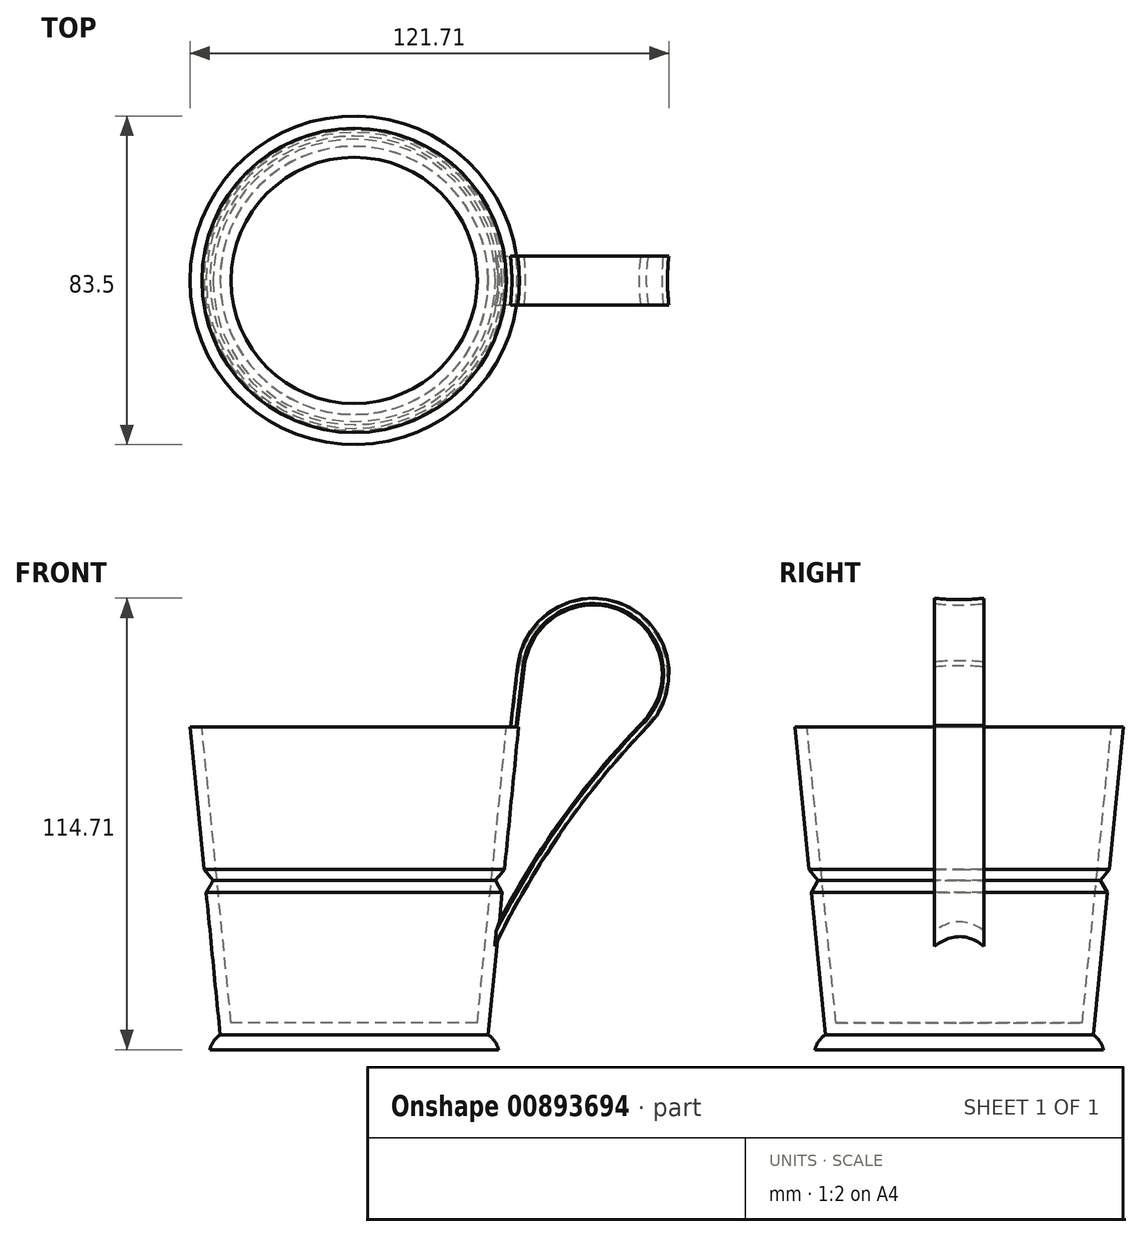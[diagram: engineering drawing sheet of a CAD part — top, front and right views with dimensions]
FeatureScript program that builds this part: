
annotation { "Feature Type Name" : "Feature", "Feature Type Description" : "" }
export const myFeature = defineFeature(function(context is Context, id is Id, definition is map)
    precondition{}
    {
        {
            var Q0;
            Q0=qCreatedBy(makeId("Top.planeOp"),FACE);
            var sketch = newSketch(context, id + "F0", { "sketchPlane" : qUnion([Q0])});
            skCircle(sketch, "E0", {"center": v(0, 0) * mm, "radius": 33.02 * mm});
            skSolve(sketch);
        }
        {
            var Q0;
            Q0=makeQuery(id+"F0.imprint","IMPRINT",FACE,{"disambiguationData":[TD([[makeQuery(id+"F0.imprint","IMPRINT",EDGE,{"derivedFrom":sQuery(id+"F0.wireOp",EDGE,"E0")}),1.0]])]});
            extrude(context, id + "F1", {"entities" : qUnion([Q0]), "depth" : 78.23 * mm, "offsetDistance" : 25.4 * mm, "hasDraft" : true, "draftAngle" : 5.63 * degree});
        }
        {
            var Q0;
            Q0=qCreatedBy(makeId("Front.planeOp"),FACE);
            var sketch = newSketch(context, id + "F2", { "sketchPlane" : qUnion([Q0])});
            skLineSegment(sketch, "E1", {"start": v(0, 0) * mm, "end": v(-34.1, 0) * mm});
            skArc(sketch, "E2", {"start": v(-34.1, 0) * mm, "mid": v(-35.73, -1.6) * mm, "end": v(-36.65, -3.7) * mm});
            skLineSegment(sketch, "E3", {"start": v(-36.65, -3.7) * mm, "end": v(0, -3.7) * mm});
            skLineSegment(sketch, "E4", {"start": v(0, -3.7) * mm, "end": v(0, 0) * mm});
            skSolve(sketch);
        }
        {
            var Q0;
            Q0=makeQuery(id+"F1.opExtrude","CAP_FACE",FACE,{"disambiguationData":[OSD([sQuery(id+"F0.wireOp",EDGE,"E0")])],"isStart":true});
            var sketch = newSketch(context, id + "F3", { "sketchPlane" : qUnion([Q0])});
            skCircle(sketch, "E5", {"center": v(0, 0) * mm, "radius": 34.04 * mm});
            skSolve(sketch);
        }
        {
            var Q0;
            Q0=makeQuery(id+"F3.imprint","IMPRINT",FACE,{"disambiguationData":[TD([[makeQuery(id+"F3.imprint","IMPRINT",EDGE,{"derivedFrom":sQuery(id+"F3.wireOp",EDGE,"E5")}),1.0]])]});
            extrude(context, id + "F4", {"entities" : qUnion([Q0]), "operationType" : NewBodyOperationType.ADD, "oppositeDirection" : true, "depth" : 78.23 * mm, "offsetDistance" : 25.4 * mm, "hasDraft" : true, "draftAngle" : 5.63 * degree});
        }
        {
            var Q0;
            {var subQ0=sQuery(id+"F0.wireOp",EDGE,"E0");Q0=makeQuery(id+"F4.boolean.opBoolean","MERGE",FACE,{"derivedFrom":[makeQuery(id+"F1.opExtrude","CAP_FACE",FACE,{"disambiguationData":[OSD([subQ0])],"isStart":false}),makeQuery(id+"F4.opExtrude","CAP_FACE",FACE,{"disambiguationData":[OSD([subQ0,sQuery(id+"F3.wireOp",EDGE,"E5")])],"isStart":false})]});}
            shell(context, id + "F5", {"entities" : qUnion([Q0]), "thickness" : 3.05 * mm});
        }
        {
            var Q0;
            Q0=qCreatedBy(makeId("Front.planeOp"),FACE);
            var sketch = newSketch(context, id + "F6", { "sketchPlane" : qUnion([Q0])});
            skLineSegment(sketch, "E6", {"start": v(0, 91.35) * mm, "end": v(0, 0) * mm});
            skLineSegment(sketch, "E7", {"start": v(5.67, 39.25) * mm, "end": v(5.67, 0.13) * mm});
            skLineSegment(sketch, "E8", {"start": v(37.88, 39.3) * mm, "end": v(35.84, 39.3) * mm});
            skLineSegment(sketch, "E9", {"start": v(35.84, 39.25) * mm, "end": v(38.45, 42.44) * mm});
            skLineSegment(sketch, "E10", {"start": v(38.45, 42.44) * mm, "end": v(37.82, 35.82) * mm});
            skLineSegment(sketch, "E11", {"start": v(37.82, 35.82) * mm, "end": v(35.84, 39.25) * mm});
            skSolve(sketch);
        }
        {
            var Q0;
            Q0 = qSketchRegion(id + "F6", true);
            var Q1;
            Q1=sQuery(id+"F6.wireOp",EDGE,"E6");
            revolve(context, id + "F7", {"operationType" : NewBodyOperationType.REMOVE, "surfaceOperationType" : NewSurfaceOperationType.NEW, "entities" : qUnion([Q0]), "axis" : qUnion([Q1]), "revolveType" : RevolveType.FULL, "oppositeDirection" : true});
        }
        {
            var Q0;
            Q0=qCreatedBy(makeId("Front.planeOp"),FACE);
            var sketch = newSketch(context, id + "F8", { "sketchPlane" : qUnion([Q0])});
            skLineSegment(sketch, "E12", {"start": v(39.9, 76.63) * mm, "end": v(42, 94) * mm});
            skArc(sketch, "E13", {"start": v(74.24, 78.63) * mm, "mid": v(68.8, 108.74) * mm, "end": v(42, 94) * mm});
            skArc(sketch, "E14", {"start": v(74.24, 78.63) * mm, "mid": v(52.38, 52.04) * mm, "end": v(35.12, 22.26) * mm});
            skSolve(sketch);
        }
        {
            var Q0;
            {var subQ0=sQuery(id+"F0.wireOp",EDGE,"E0");Q0=makeQuery(id+"F4.boolean.opBoolean","MERGE",FACE,{"derivedFrom":[makeQuery(id+"F1.opExtrude","CAP_FACE",FACE,{"disambiguationData":[OSD([subQ0])],"isStart":false}),makeQuery(id+"F4.opExtrude","CAP_FACE",FACE,{"disambiguationData":[OSD([subQ0,sQuery(id+"F3.wireOp",EDGE,"E5")])],"isStart":false})]});}
            var sketch = newSketch(context, id + "F9", { "sketchPlane" : qUnion([Q0])});
            skPoint(sketch, "E15.end.orphan", {"position": v(40.77, 6.35) * mm});
            skPoint(sketch, "E16.end.orphan", {"position": v(40.77, -6.34) * mm});
            skPoint(sketch, "E16.start.orphan", {"position": v(40.77, 0) * mm});
            skPoint(sketch, "E17.orphan", {"position": v(45.85, 6.35) * mm});
            skPoint(sketch, "E18.orphan", {"position": v(37.55, -6.34) * mm});
            skArc(sketch, "E19", {"start": v(74.42, 6.23) * mm, "mid": v(73.92, -0.05) * mm, "end": v(74.44, -6.34) * mm});
            skArc(sketch, "E20", {"start": v(72.52, 6.23) * mm, "mid": v(72.04, -0.05) * mm, "end": v(72.54, -6.34) * mm});
            skLineSegment(sketch, "E21.trimOffspring", {"start": v(74.44, -6.34) * mm, "end": v(72.54, -6.34) * mm});
            skLineSegment(sketch, "E22.trimOffspring", {"start": v(74.42, 6.23) * mm, "end": v(72.52, 6.23) * mm});
            skSolve(sketch);
        }
        {
            var Q0;
            Q0 = qSketchRegion(id + "F9", true);
            var Q1;
            Q1=sQuery(id+"F8.wireOp",EDGE,"E14");
            var Q2;
            Q2=sQuery(id+"F8.wireOp",EDGE,"E13");
            var Q3;
            Q3=sQuery(id+"F8.wireOp",EDGE,"E12");
            sweep(context, id + "F10", {"operationType" : NewBodyOperationType.ADD, "profiles" : qUnion([Q0]), "path" : qUnion([Q1, Q2, Q3])});
        }
        {
            var Q0;
            Q0=makeQuery(id+"F2.imprint","IMPRINT",FACE,{"disambiguationData":[TD([[makeQuery(id+"F2.imprint","IMPRINT",EDGE,{"derivedFrom":sQuery(id+"F2.wireOp",EDGE,"E1")}),1.0]])]});
            var Q1;
            Q1=sQuery(id+"F2.wireOp",EDGE,"E4");
            revolve(context, id + "F11", {"operationType" : NewBodyOperationType.ADD, "surfaceOperationType" : NewSurfaceOperationType.NEW, "entities" : qUnion([Q0]), "axis" : qUnion([Q1]), "revolveType" : RevolveType.FULL});
        }
    });
